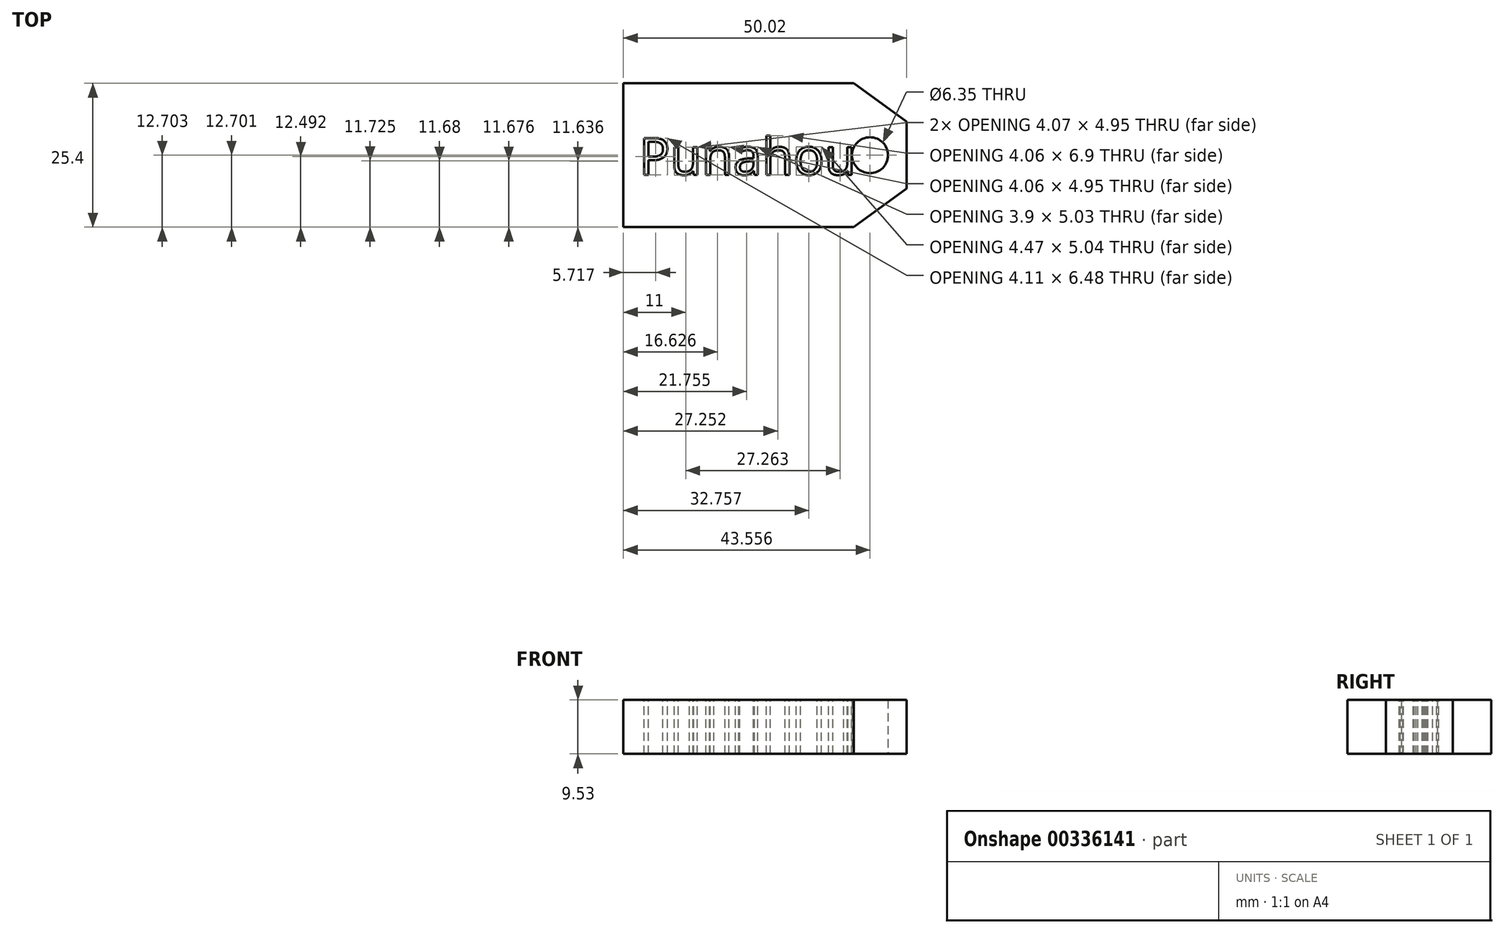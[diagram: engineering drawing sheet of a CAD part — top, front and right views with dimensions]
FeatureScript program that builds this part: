
annotation { "Feature Type Name" : "Feature", "Feature Type Description" : "" }
export const myFeature = defineFeature(function(context is Context, id is Id, definition is map)
    precondition{}
    {
        {
            var Q0;
            Q0=qCreatedBy(makeId("Top.planeOp"),FACE);
            var sketch = newSketch(context, id + "F0", { "sketchPlane" : qUnion([Q0])});
            skLineSegment(sketch, "E0", {"start": v(-15.27, -25.73) * mm, "end": v(-15.27, -38.43) * mm});
            skLineSegment(sketch, "E1", {"start": v(-15.27, -38.43) * mm, "end": v(25.4, -38.43) * mm});
            skLineSegment(sketch, "E2", {"start": v(25.4, -38.43) * mm, "end": v(34.75, -31.63) * mm});
            skLineSegment(sketch, "E3", {"start": v(34.75, -31.63) * mm, "end": v(34.75, -25.73) * mm});
            skLineSegment(sketch, "E4", {"start": v(-22.5, -25.73) * mm, "end": v(40.66, -25.73) * mm, "construction": true});
            skLineSegment(sketch, "E5.MirrorCS", {"start": v(-15.27, -25.73) * mm, "end": v(-15.27, -13.03) * mm});
            skLineSegment(sketch, "E6.MirrorCS", {"start": v(-15.27, -13.03) * mm, "end": v(25.4, -13.03) * mm});
            skLineSegment(sketch, "E7.MirrorCS", {"start": v(25.4, -13.03) * mm, "end": v(34.75, -19.82) * mm});
            skLineSegment(sketch, "E8.MirrorCS", {"start": v(34.75, -19.82) * mm, "end": v(34.75, -25.73) * mm});
            skCircle(sketch, "E9", {"center": v(28.29, -25.73) * mm, "radius": 3.18 * mm});
            skSolve(sketch);
        }
        {
            var Q0;
            Q0=makeQuery(id+"F0.imprint","IMPRINT",FACE,{"disambiguationData":[TD([[makeQuery(id+"F0.imprint","IMPRINT",EDGE,{"derivedFrom":sQuery(id+"F0.wireOp",EDGE,"E0")}),1.0]])]});
            extrude(context, id + "F1", {"entities" : qUnion([Q0]), "depth" : 9.52 * mm});
        }
        {
            var Q0;
            Q0=makeQuery(id+"F1.opExtrude","CAP_FACE",FACE,{"disambiguationData":[OSD([sQuery(id+"F0.wireOp",EDGE,"E0"),sQuery(id+"F0.wireOp",EDGE,"E1"),sQuery(id+"F0.wireOp",EDGE,"E2"),sQuery(id+"F0.wireOp",EDGE,"E3"),sQuery(id+"F0.wireOp",EDGE,"E5.MirrorCS"),sQuery(id+"F0.wireOp",EDGE,"E6.MirrorCS"),sQuery(id+"F0.wireOp",EDGE,"E7.MirrorCS"),sQuery(id+"F0.wireOp",EDGE,"E8.MirrorCS"),sQuery(id+"F0.wireOp",EDGE,"E9")])],"isStart":false});
            var sketch = newSketch(context, id + "F2", { "sketchPlane" : qUnion([Q0])});
            skText(sketch, "E10", { "text": "Punahou", "fontName": "OpenSans-Regular.ttf"});
            const initialGuessF2  = {"E10": [-0.0125, -0.02918, 1, 0, 0.00654]};
            skSetInitialGuess(sketch, initialGuessF2);
            skSolve(sketch);
        }
        {
            var Q0;
            Q0 = qSketchRegion(id + "F2", true);
            extrude(context, id + "F3", {"entities" : qUnion([Q0]), "operationType" : NewBodyOperationType.REMOVE, "oppositeDirection" : true, "depth" : 25.4 * mm});
        }
    });
